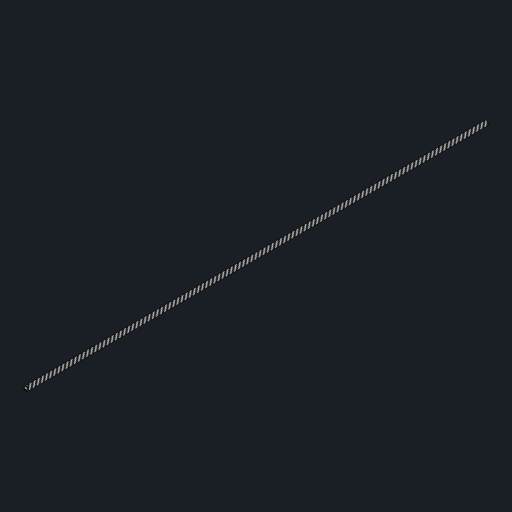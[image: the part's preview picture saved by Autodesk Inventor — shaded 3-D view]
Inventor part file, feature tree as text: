
AUTODESK INVENTOR PART (.ipt)
format: ipt  version: 2023 (Build 270158000, 158)  size: 91,136 bytes
history: native  units: mm
features: other x1, extrude x1, sketch x1
ambient origin geometry x8: Origin, YZ Plane, XZ Plane, XY Plane, X Axis, Y Axis, Z Axis, Center Point
bodies: Body1 (feature_tree)
feature tree (3):
  other  "ソリッド1"
  extrude  "押し出し1"  Depth=3.0mm
  sketch  "スケッチ1"
